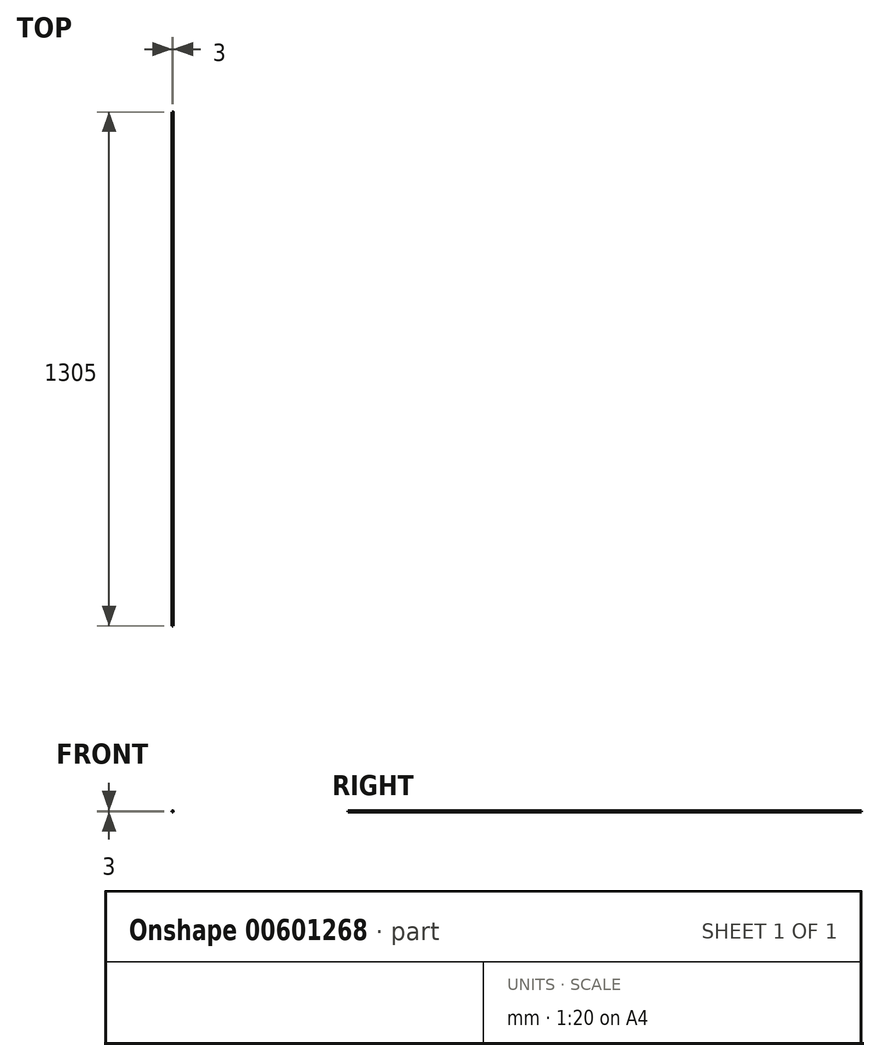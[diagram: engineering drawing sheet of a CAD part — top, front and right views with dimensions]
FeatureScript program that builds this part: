
annotation { "Feature Type Name" : "Feature", "Feature Type Description" : "" }
export const myFeature = defineFeature(function(context is Context, id is Id, definition is map)
    precondition{}
    {
        {
            var Q0;
            Q0=qCreatedBy(makeId("Front.planeOp"),FACE);
            var sketch = newSketch(context, id + "F0", { "sketchPlane" : qUnion([Q0])});
            skCircle(sketch, "E0", {"center": v(0, 0) * mm, "radius": 1.5 * mm});
            skSolve(sketch);
        }
        {
            var Q0;
            Q0=makeQuery(id+"F0.imprint","IMPRINT",FACE,{"disambiguationData":[TD([[makeQuery(id+"F0.imprint","IMPRINT",EDGE,{"derivedFrom":sQuery(id+"F0.wireOp",EDGE,"E0")}),1.0]])]});
            extrude(context, id + "F1", {"entities" : qUnion([Q0]), "depth" : 1305 * mm, "offsetDistance" : 25 * mm});
        }
    });
